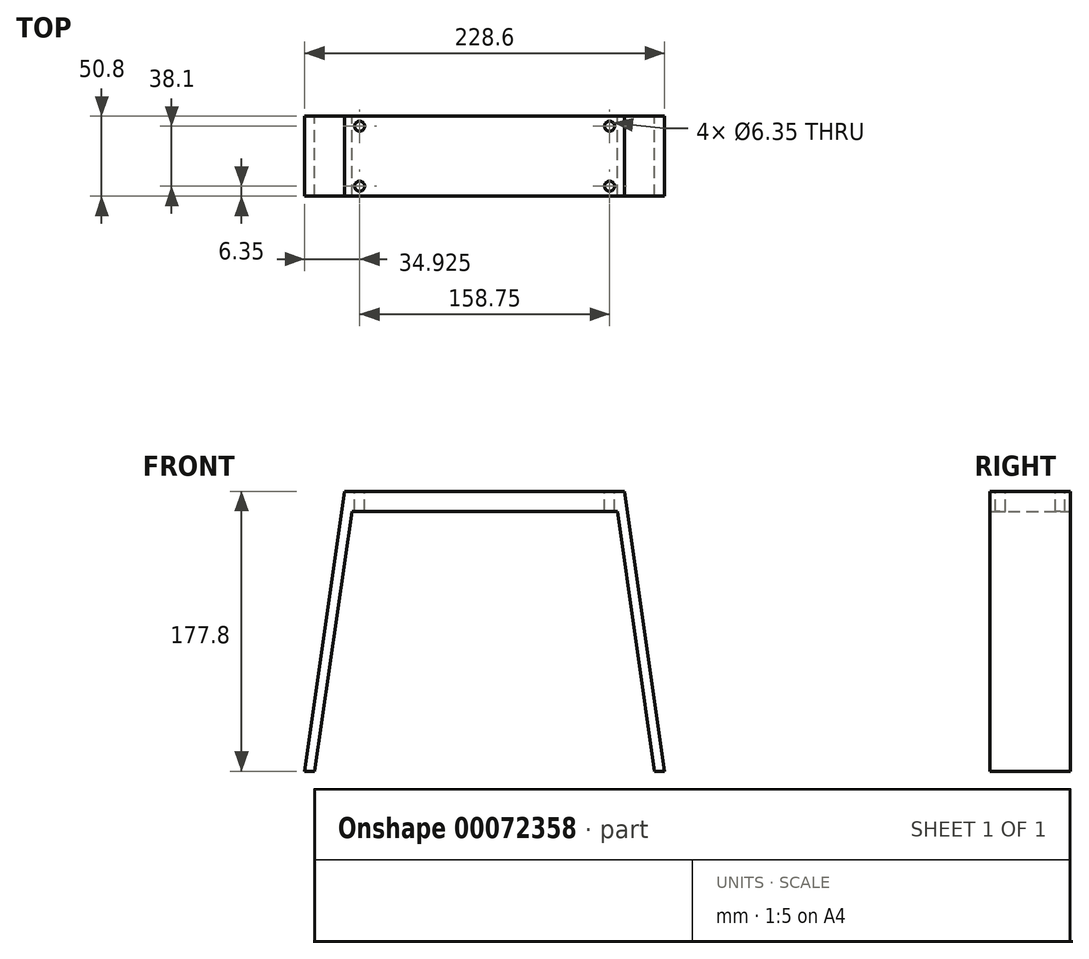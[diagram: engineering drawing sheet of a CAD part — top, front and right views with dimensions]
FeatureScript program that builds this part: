
annotation { "Feature Type Name" : "Feature", "Feature Type Description" : "" }
export const myFeature = defineFeature(function(context is Context, id is Id, definition is map)
    precondition{}
    {
        {
            var Q0;
            Q0=qCreatedBy(makeId("Front.planeOp"),FACE);
            var sketch = newSketch(context, id + "F0", { "sketchPlane" : qUnion([Q0])});
            skLineSegment(sketch, "E0", {"start": v(0, 0) * mm, "end": v(25.4, 177.8) * mm});
            skLineSegment(sketch, "E1", {"start": v(25.4, 177.8) * mm, "end": v(203.2, 177.8) * mm});
            skLineSegment(sketch, "E2", {"start": v(203.2, 177.8) * mm, "end": v(228.6, 0) * mm});
            skLineSegment(sketch, "E3", {"start": v(228.6, 0) * mm, "end": v(222.19, 0) * mm});
            skLineSegment(sketch, "E4", {"start": v(222.19, 0) * mm, "end": v(198.6, 165.1) * mm});
            skLineSegment(sketch, "E5", {"start": v(198.6, 165.1) * mm, "end": v(30, 165.1) * mm});
            skLineSegment(sketch, "E6", {"start": v(30, 165.1) * mm, "end": v(6.41, 0) * mm});
            skLineSegment(sketch, "E7", {"start": v(6.41, 0) * mm, "end": v(0, 0) * mm});
            skSolve(sketch);
        }
        {
            var Q0;
            Q0=makeQuery(id+"F0.imprint","IMPRINT",FACE,{"disambiguationData":[TD([[makeQuery(id+"F0.imprint","IMPRINT",EDGE,{"derivedFrom":sQuery(id+"F0.wireOp",EDGE,"E0")}),-1.0]])]});
            extrude(context, id + "F1", {"entities" : qUnion([Q0]), "depth" : 50.8 * mm});
        }
        {
            var Q0;
            Q0=makeQuery(id+"F1.opExtrude","SWEPT_BODY",BODY,{"disambiguationData":[OSD([sQuery(id+"F0.wireOp",EDGE,"E0"),sQuery(id+"F0.wireOp",EDGE,"E1"),sQuery(id+"F0.wireOp",EDGE,"E2"),sQuery(id+"F0.wireOp",EDGE,"E3"),sQuery(id+"F0.wireOp",EDGE,"E4"),sQuery(id+"F0.wireOp",EDGE,"E5"),sQuery(id+"F0.wireOp",EDGE,"E6"),sQuery(id+"F0.wireOp",EDGE,"E7")])]});
            transform(context, id + "F2", {"entities" : qUnion([Q0]), "transformType" : TransformType.TRANSLATION_3D, "dx" : -114.3 * mm, "dy" : 0 * mm, "dz" : 0 * mm, "makeCopy" : false});
        }
        {
            var Q0;
            Q0=makeQuery(id+"F1.opExtrude","SWEPT_FACE",FACE,{"disambiguationData":[OSD([sQuery(id+"F0.wireOp",EDGE,"E1")])]});
            var sketch = newSketch(context, id + "F3", { "sketchPlane" : qUnion([Q0])});
            skCircle(sketch, "E8", {"center": v(-79.37, -6.35) * mm, "radius": 3.18 * mm});
            skCircle(sketch, "E9", {"center": v(-79.37, -44.45) * mm, "radius": 3.18 * mm});
            skCircle(sketch, "E10", {"center": v(79.38, -6.35) * mm, "radius": 3.18 * mm});
            skCircle(sketch, "E11", {"center": v(79.38, -44.45) * mm, "radius": 3.18 * mm});
            skSolve(sketch);
        }
        {
            var Q0;
            Q0 = qSketchRegion(id + "F3", true);
            extrude(context, id + "F4", {"entities" : qUnion([Q0]), "operationType" : NewBodyOperationType.REMOVE, "endBound" : BoundingType.THROUGH_ALL, "oppositeDirection" : true, "depth" : 25.4 * mm});
        }
    });
